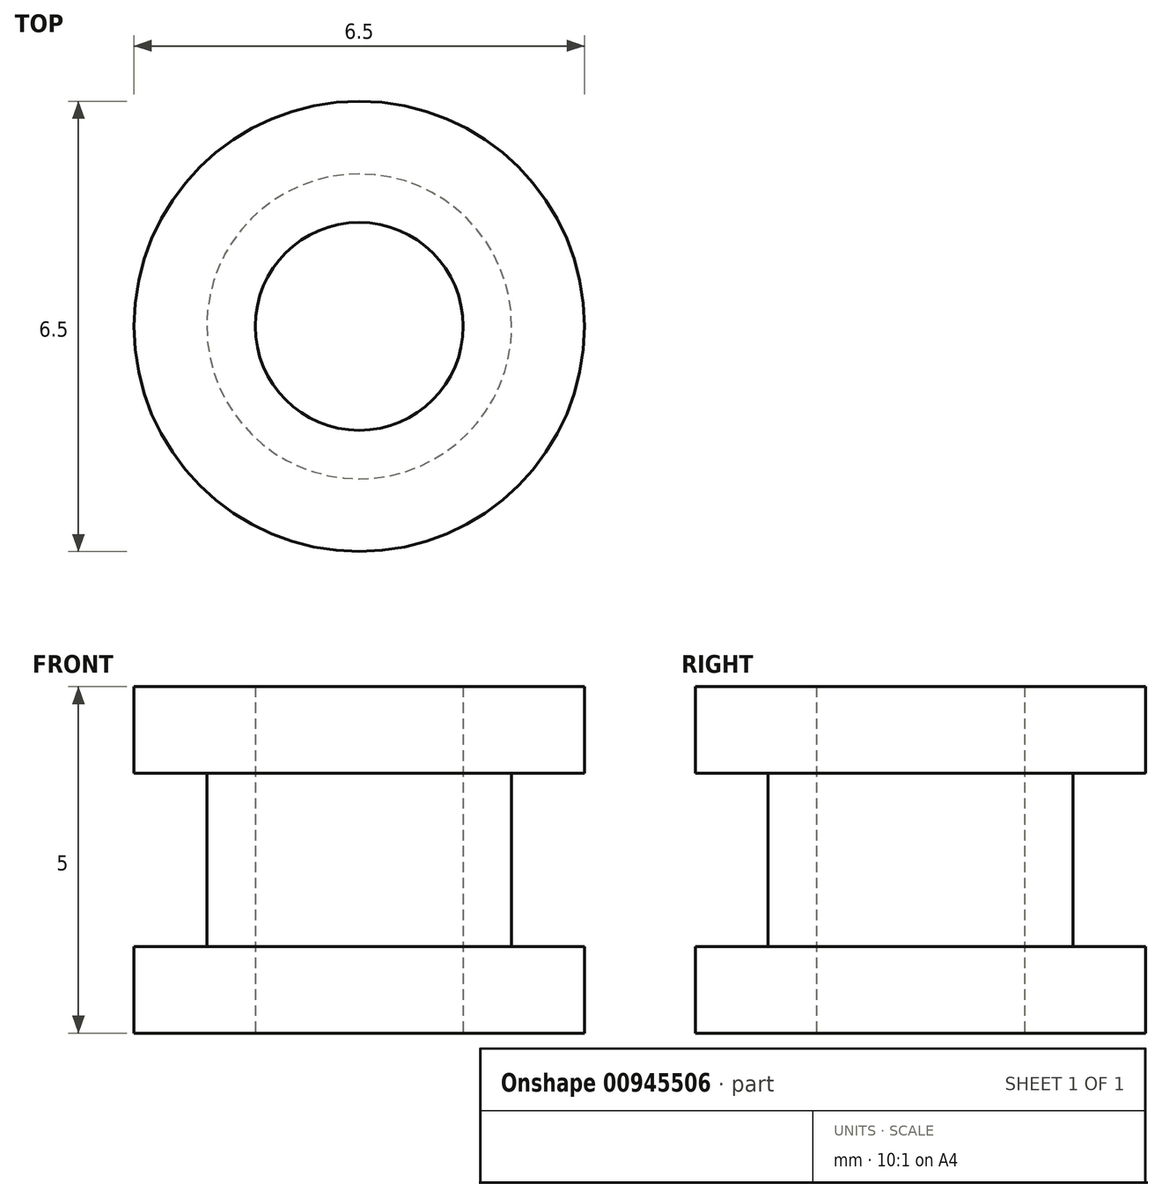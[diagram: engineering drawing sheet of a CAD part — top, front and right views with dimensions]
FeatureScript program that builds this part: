
annotation { "Feature Type Name" : "Feature", "Feature Type Description" : "" }
export const myFeature = defineFeature(function(context is Context, id is Id, definition is map)
    precondition{}
    {
        {
            var Q0;
            Q0=qCreatedBy(makeId("Top.planeOp"),FACE);
            var sketch = newSketch(context, id + "F0", { "sketchPlane" : qUnion([Q0])});
            skCircle(sketch, "E0", {"center": v(0, 0) * mm, "radius": 2.2 * mm});
            skCircle(sketch, "E1", {"center": v(0, 0) * mm, "radius": 1.5 * mm});
            skSolve(sketch);
        }
        {
            var Q0;
            Q0 = qSketchRegion(id + "F0", true);
            extrude(context, id + "F1", {"entities" : qUnion([Q0]), "depth" : (2.5 / 2) * mm, "offsetDistance" : 25 * mm});
        }
        {
            var Q0;
            Q0=makeQuery(id+"F1.opExtrude","CAP_FACE",FACE,{"disambiguationData":[OSD([sQuery(id+"F0.wireOp",EDGE,"E0"),sQuery(id+"F0.wireOp",EDGE,"E1")])],"isStart":false});
            var sketch = newSketch(context, id + "F2", { "sketchPlane" : qUnion([Q0])});
            skCircle(sketch, "E2", {"center": v(0, 0) * mm, "radius": 3.25 * mm});
            skCircle(sketch, "E3", {"center": v(0, 0) * mm, "radius": 1.5 * mm});
            skSolve(sketch);
        }
        {
            var Q0;
            Q0 = qSketchRegion(id + "F2", true);
            extrude(context, id + "F3", {"entities" : qUnion([Q0]), "operationType" : NewBodyOperationType.ADD, "depth" : 1.25 * mm, "offsetDistance" : 25 * mm});
        }
        {
            var Q0;
            Q0=makeQuery(id+"F1.opExtrude","SWEPT_BODY",BODY,{"disambiguationData":[OSD([sQuery(id+"F0.wireOp",EDGE,"E0"),sQuery(id+"F0.wireOp",EDGE,"E1")])]});
            var Q1;
            Q1=qCreatedBy(makeId("Top.planeOp"),FACE);
            mirror(context, id + "F4", {"operationType" : NewBodyOperationType.ADD, "entities" : qUnion([Q0]), "mirrorPlane" : qUnion([Q1])});
        }
    });
